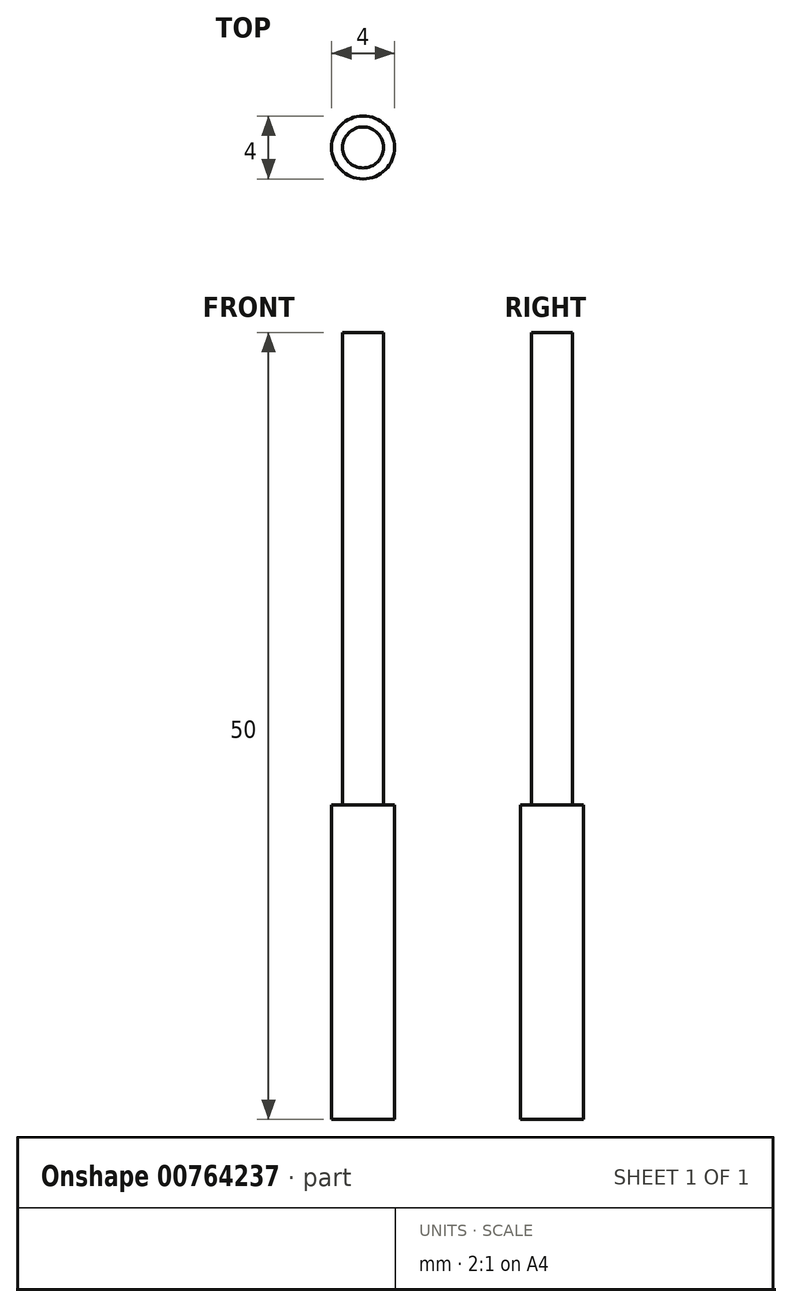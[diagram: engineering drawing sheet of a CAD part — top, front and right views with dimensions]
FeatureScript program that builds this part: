
annotation { "Feature Type Name" : "Feature", "Feature Type Description" : "" }
export const myFeature = defineFeature(function(context is Context, id is Id, definition is map)
    precondition{}
    {
        {
            var Q0;
            Q0=qCreatedBy(makeId("Front.planeOp"),FACE);
            var sketch = newSketch(context, id + "F0", { "sketchPlane" : qUnion([Q0])});
            skPoint(sketch, "E0.middle", {"position": v(0, 0) * mm});
            skLineSegment(sketch, "E1", {"start": v(0, 30) * mm, "end": v(1.3, 30) * mm});
            skLineSegment(sketch, "E2", {"start": v(1.3, 30) * mm, "end": v(1.3, 0) * mm});
            skLineSegment(sketch, "E3", {"start": v(1.3, 0) * mm, "end": v(2, 0) * mm});
            skLineSegment(sketch, "E4", {"start": v(2, 0) * mm, "end": v(2, -20) * mm});
            skLineSegment(sketch, "E5", {"start": v(2, -20) * mm, "end": v(0, -20) * mm});
            skLineSegment(sketch, "E6", {"start": v(0, -20) * mm, "end": v(0, 30) * mm});
            skSolve(sketch);
        }
        {
            var Q0;
            Q0 = qSketchRegion(id + "F0", true);
            var Q1;
            Q1=sQuery(id+"F0.wireOp",EDGE,"E6");
            revolve(context, id + "F1", {"surfaceOperationType" : NewSurfaceOperationType.NEW, "entities" : qUnion([Q0]), "axis" : qUnion([Q1]), "revolveType" : RevolveType.FULL});
        }
    });
